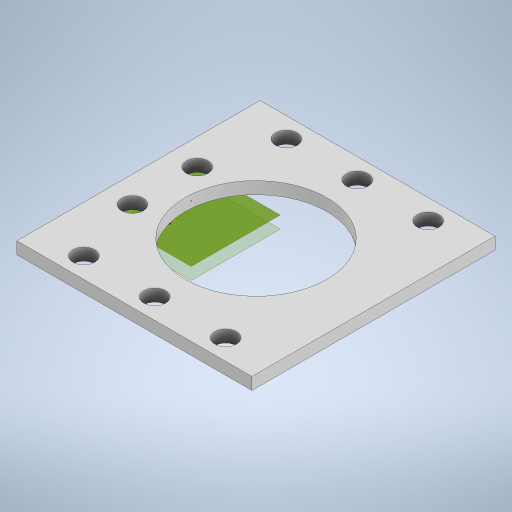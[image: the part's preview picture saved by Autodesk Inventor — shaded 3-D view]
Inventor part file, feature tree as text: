
AUTODESK INVENTOR PART (.ipt)
format: ipt  version: 2024 (Build 280153000, 153)  size: 307,712 bytes
history: native  units: mm
features: plane x7, sketch x5, extrude x4
ambient origin geometry x8: Origin, YZ Plane, XZ Plane, XY Plane, X Axis, Y Axis, Z Axis, Center Point
bodies: Body1 (feature_tree)
feature tree (16):
  plane  "Work Plane5"
  plane  "Work Plane2"
  plane  "Work Plane1"
  plane  "Work Plane7"
  sketch  "Sketch77"  dims[d219=35.0mm d220=58.0mm]
  plane  "Work Plane6"
  extrude  "Extrusion53"  Depth=58.0mm
  extrude  "Extrusion54"  Depth=3.0mm TaperAngle=0.0deg
  plane  "Work Plane9"
  extrude  "Extrusion56"  Depth=3.0mm
  plane  "Work Plane8"
  extrude  "Extrusion57"  Depth=5.4mm
  sketch  "Sketch84"  dims[d235=17.5mm d236=5.4mm d237=17.5mm d238=5.4mm d239=5.0mm d240=17.0mm d241=5.4mm d242=16.0mm d243=5.4mm d244=17.0mm d245=5.4mm d246=17.5mm d247=5.4mm d248=17.5mm d249=5.0mm d250=30.0mm d251=0.0mm d253=4.8mm d254=4.5mm d255=0.0mm d49=0.5mm d50=0.872665mm d51=0.5mm d52=0.872665mm d130=0.5mm d131=0.872665mm d132=0.5mm d133=0.872665mm d156=0.5mm d157=0.872665mm d158=0.5mm d159=0.872665mm d173=0.5mm d174=0.872665mm d175=0.5mm d176=0.872665mm d226=0.5mm d227=0.872665mm]
  sketch  "Sketch78"  dims[d221=60.0mm d222=3.0mm d223=0.0mm]
  sketch  "Sketch81"  dims[d224=3.0mm d225=0.0mm d232=5.0mm]
  sketch  "Sketch83"  dims[d233=11.5mm d234=5.4mm]
